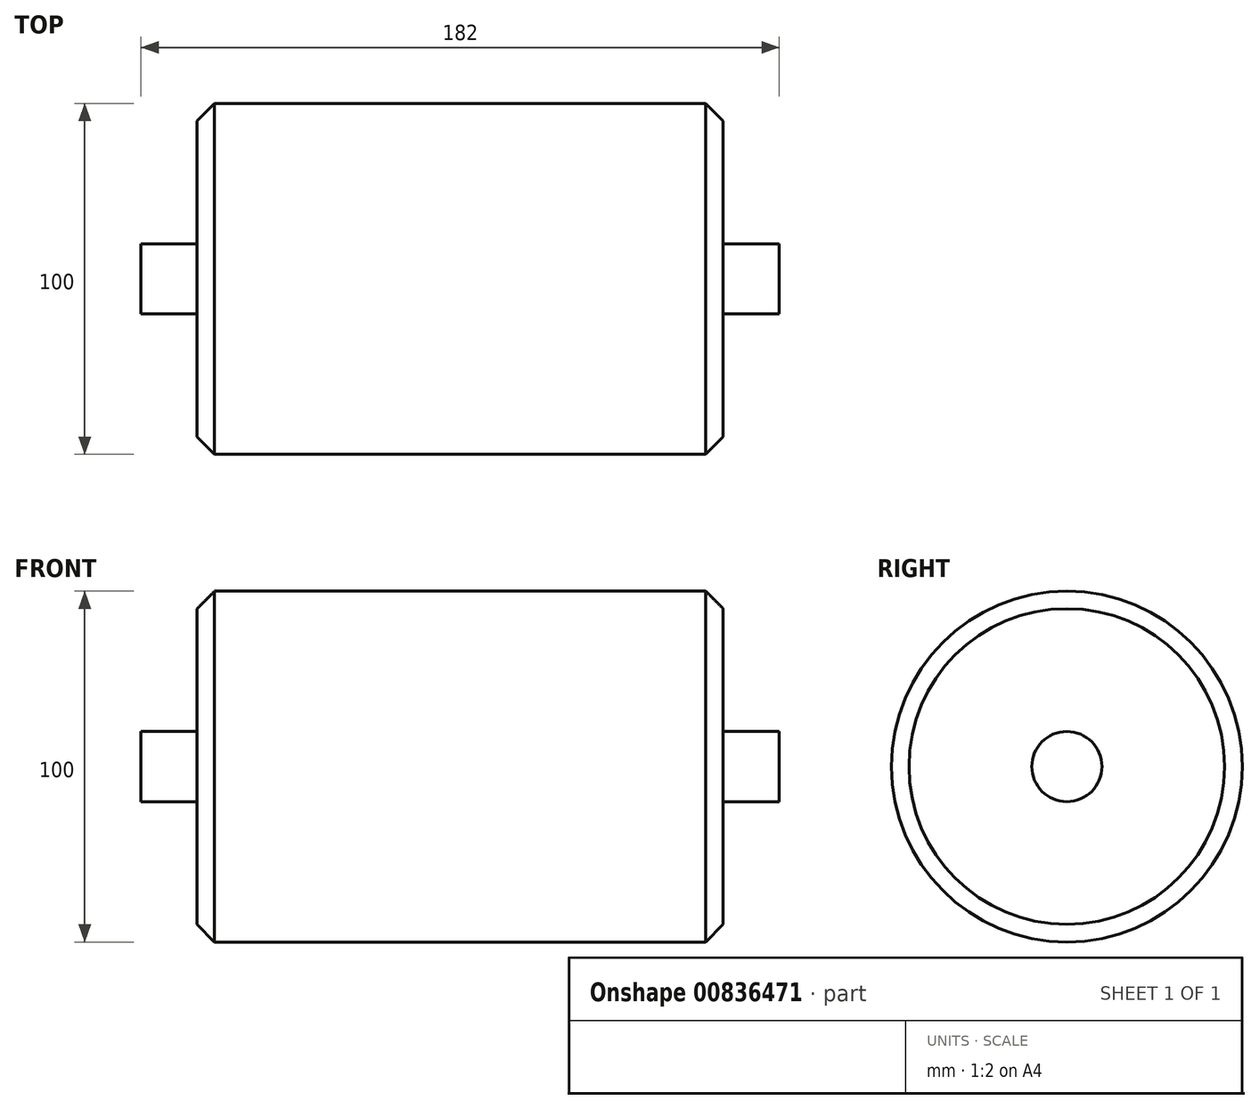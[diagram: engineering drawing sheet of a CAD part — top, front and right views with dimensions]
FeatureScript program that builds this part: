
annotation { "Feature Type Name" : "Feature", "Feature Type Description" : "" }
export const myFeature = defineFeature(function(context is Context, id is Id, definition is map)
    precondition{}
    {
        {
            var Q0;
            Q0=qCreatedBy(makeId("Front.planeOp"),FACE);
            var sketch = newSketch(context, id + "F0", { "sketchPlane" : qUnion([Q0])});
            skLineSegment(sketch, "E0.top", {"start": v(0, 100) * mm, "end": v(150, 100) * mm});
            skLineSegment(sketch, "E0.right", {"start": v(150, 50) * mm, "end": v(150, 100) * mm});
            skLineSegment(sketch, "E1", {"start": v(-28.96, 50) * mm, "end": v(207.18, 50) * mm});
            skLineSegment(sketch, "E2.top", {"start": v(0, 60) * mm, "end": v(-16, 60) * mm});
            skLineSegment(sketch, "E2.left", {"start": v(0, 50) * mm, "end": v(0, 60) * mm});
            skLineSegment(sketch, "E2.right", {"start": v(-16, 50) * mm, "end": v(-16, 60) * mm});
            skLineSegment(sketch, "E3.MirrorCS", {"start": v(150, 60) * mm, "end": v(166, 60) * mm});
            skLineSegment(sketch, "E4.MirrorCS", {"start": v(166, 50) * mm, "end": v(166, 60) * mm});
            skLineSegment(sketch, "E5.trimOffspring", {"start": v(0, 50) * mm, "end": v(0, 100) * mm});
            skSolve(sketch);
        }
        {
            var Q0;
            Q0 = qSketchRegion(id + "F0", true);
            var Q1;
            Q1=sQuery(id+"F0.wireOp",EDGE,"E1");
            revolve(context, id + "F1", {"surfaceOperationType" : NewSurfaceOperationType.NEW, "entities" : qUnion([Q0]), "axis" : qUnion([Q1]), "revolveType" : RevolveType.FULL});
        }
        {
            var Q0;
            Q0=makeQuery(id+"F1.opRevolve","SWEPT_FACE",FACE,{"disambiguationData":[OSD([sQuery(id+"F0.wireOp",EDGE,"E0.top")])]});
            chamfer(context, id + "F2", {"entities" : qUnion([Q0]), "chamferType" : ChamferType.OFFSET_ANGLE, "width" : 5 * mm, "oppositeDirection" : false, "angle" : 45 * degree, "tangentPropagation" : true});
        }
    });
